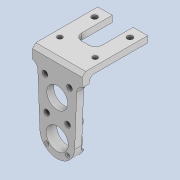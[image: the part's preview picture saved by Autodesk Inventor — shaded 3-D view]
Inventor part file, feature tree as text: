
AUTODESK INVENTOR PART (.ipt)
format: ipt  version: 2020 (Build 240168000, 168)  size: 375,296 bytes
history: native  units: mm
features: reference x12, projected_geometry x12, sketch x10, extrude x9, fillet x6, other x6, chamfer x1, hole x1, thicken_offset x1
ambient origin geometry x8: Origin, YZ Plane, XZ Plane, XY Plane, X Axis, Y Axis, Z Axis, Center Point
bodies: Solid1 (feature_tree)
feature tree (58):
  extrude  "Extrusion1"  Depth=6.0mm
  extrude  "Extrusion2"  Depth=10.0mm
  extrude  "Extrusion3"  Depth=1.5mm
  extrude  "Extrusion4"  Depth=2.0mm
  extrude  "Extrusion5"  Depth=4.15mm
  extrude  "Extrusion6"  Depth=1.8mm TaperAngle=0.0deg
  extrude  "Extrusion7"  Depth=3.0mm TaperAngle=0.0deg
  fillet  "Fillet1"  Radius=3.0mm
  fillet  "Fillet2"  Radius=1.6mm
  chamfer  "Chamfer1"  Distance=6.0mm
  fillet  "Fillet3"  Radius=8.5mm
  fillet  "Fillet4"  Radius=1.0mm
  fillet  "Fillet5"  Radius=1.0mm
  extrude  "Extrusion8"  Depth=1.0mm
  hole  "Hole1"  [1 undecoded]
  fillet  "Fillet6"  Radius=1.0mm
  extrude  "Extrusion9"  Depth=1.5mm
  thicken_offset  "Thicken1"
  sketch  "Sketch1"  dims[d0=6.0mm d1=6.0mm]
  reference  "Reference1"
  reference  "Reference2"
  reference  "Reference3"
  reference  "Reference4"
  reference  "Reference5"
  sketch  "Sketch2"  dims[d2=8.5mm d3=10.0mm]
  projected_geometry  "Projected Loop1"
  reference  "Reference6"
  sketch  "Sketch3"  dims[d4=1.5mm d5=1.5mm]
  reference  "Reference7"
  projected_geometry  "Projected Loop2"
  projected_geometry  "Projected Loop3"
  projected_geometry  "Projected Loop4"
  sketch  "Sketch4"  dims[d6=2.0mm d7=0.0mm d8=4.15mm]
  projected_geometry  "Projected Loop5"
  sketch  "Sketch5"  dims[d9=18.8mm d10=4.15mm]
  projected_geometry  "Projected Loop6"
  reference  "Reference8"
  reference  "Reference9"
  sketch  "Sketch6"  dims[d11=18.8mm d12=1.8mm d13=0.0mm]
  reference  "Reference10"
  sketch  "Sketch7"  dims[d14=17.5mm d15=6.0mm d16=0.0mm d17=3.0mm d18=1.6mm]
  reference  "Reference11"
  reference  "Reference12"
  sketch  "Sketch8"  dims[d19=3.0mm]
  projected_geometry  "Projected Loop7"
  sketch  "Sketch9"  dims[d20=1.6mm d21=6.0mm d22=0.0mm d23=8.5mm d24=1.0mm d25=0.0mm d26=1.0mm d27=0.0mm]
  projected_geometry  "Projected Loop8"
  projected_geometry  "Projected Loop9"
  projected_geometry  "Projected Loop10"
  sketch  "Sketch10"  dims[d28=5.0mm d29=0.0mm d30=1.0mm d31=1.5mm d32=1.0mm d33=2.0mm d34=45.0deg d35=1.5mm d36=2.0mm d37=2.0mm d38=6.0mm d39=6.0mm d40=30.0deg d41=30.0deg d42=5.5mm d43=5.5mm d44=6.981317mm d45=6.981317mm d46=3.0mm d47=3.0mm d48=3.0mm d49=3.0mm d50=3.0mm d51=3.0mm d52=1.0mm d53=0.0mm d54=1.6mm d55=6.0mm d56=4.0mm d57=2.0mm d58=90.0deg d59=5.0mm d60=0.0mm d61=1.0mm d62=10.15mm d63=10.0mm d64=1.4mm d65=1.4mm d66=3.0mm d67=0.0mm d68=0.15mm d69=0.15mm]
  projected_geometry  "Projected Loop11"
  projected_geometry  "Projected Loop12"
  parser-record x1  (decoder bookkeeping rows leaked as tree rows — omitted from the tree; the rows remain in map.json)
  other  "tip_ass_t1.iam"
  other  "motor_1608:1"
  other  "motor_1608_outer:1"
  other  "bearing_3_6_2:3"
  other  "pin_conn_1:1"
note: 1 required parameter value undecoded (feature->parameter linkage not recoverable at this tier; creation-order binding heuristic only, values carry confidence <= 0.55)
note: 1 file-system path scrubbed to <path> (originals preserved in map.json)
